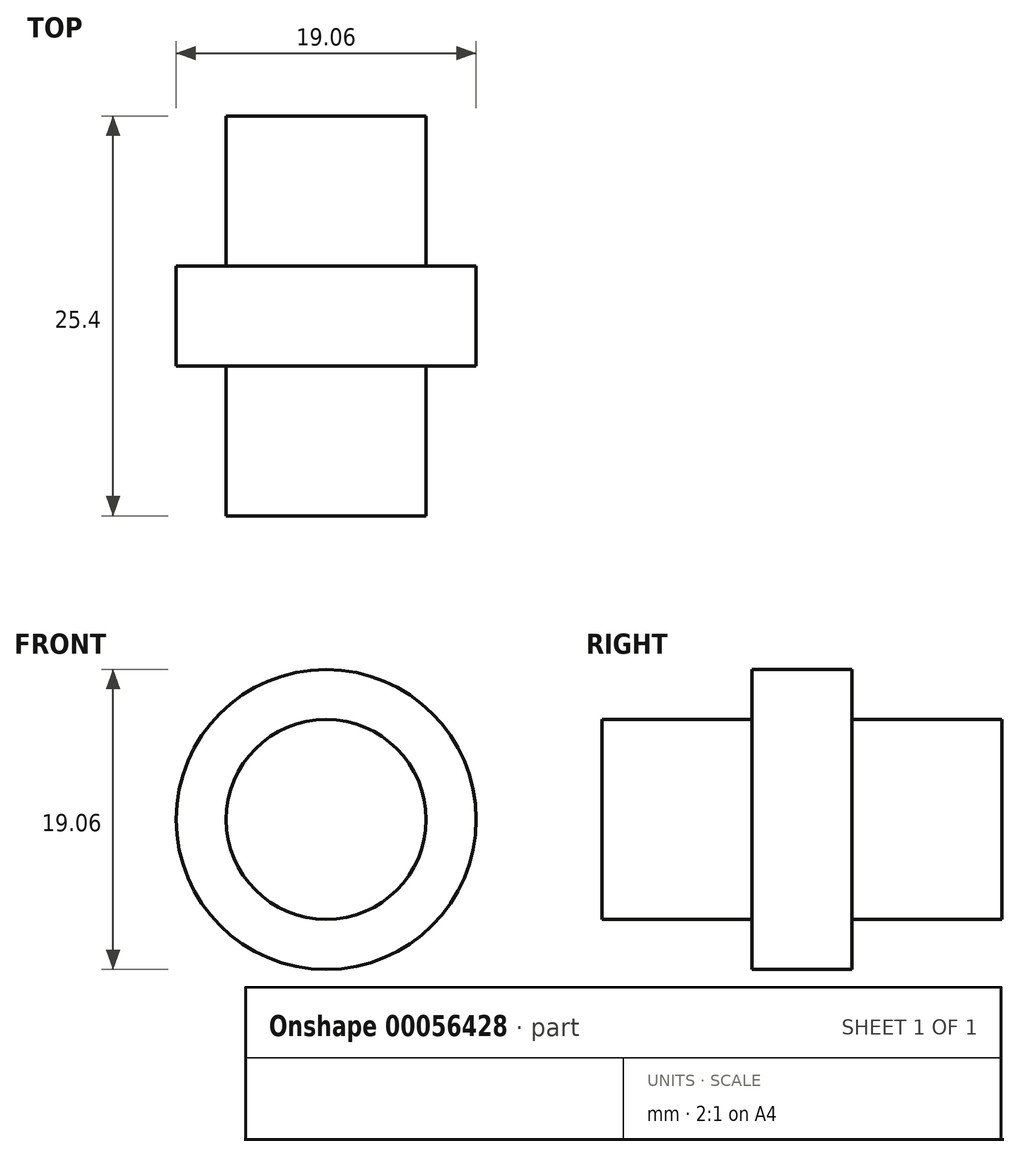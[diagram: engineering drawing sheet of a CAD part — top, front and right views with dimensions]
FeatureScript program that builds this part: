
annotation { "Feature Type Name" : "Feature", "Feature Type Description" : "" }
export const myFeature = defineFeature(function(context is Context, id is Id, definition is map)
    precondition{}
    {
        {
            var Q0;
            Q0=qCreatedBy(makeId("Front.planeOp"),FACE);
            var sketch = newSketch(context, id + "F0", { "sketchPlane" : qUnion([Q0])});
            skCircle(sketch, "E0", {"center": v(0, 0) * mm, "radius": 6.35 * mm});
            skCircle(sketch, "E1", {"center": v(0, 0) * mm, "radius": 9.53 * mm});
            skSolve(sketch);
        }
        {
            var Q0;
            Q0=makeQuery(id+"F0.imprint","IMPRINT",FACE,{"disambiguationData":[TD([[makeQuery(id+"F0.imprint","IMPRINT",EDGE,{"derivedFrom":sQuery(id+"F0.wireOp",EDGE,"E0")}),1.0]])]});
            extrude(context, id + "F1", {"entities" : qUnion([Q0]), "endBound" : BoundingType.SYMMETRIC, "depth" : 25.4 * mm});
        }
        {
            var Q0;
            Q0 = qSketchRegion(id + "F0", true);
            extrude(context, id + "F2", {"entities" : qUnion([Q0]), "operationType" : NewBodyOperationType.ADD, "endBound" : BoundingType.SYMMETRIC, "depth" : 6.35 * mm});
        }
    });
